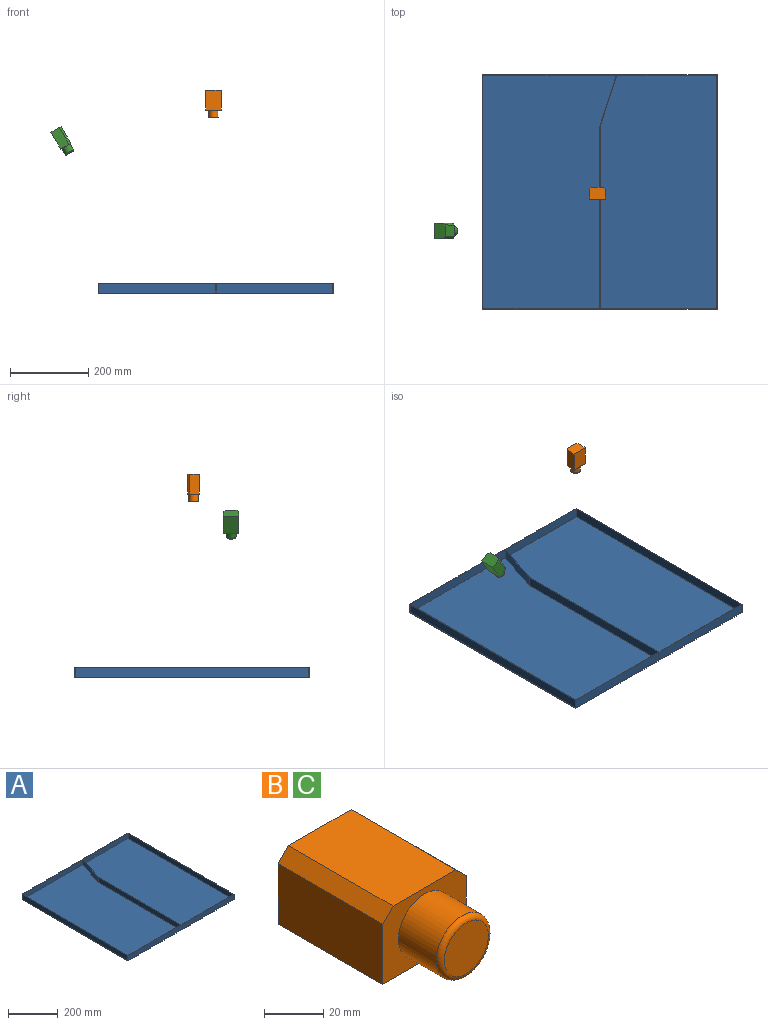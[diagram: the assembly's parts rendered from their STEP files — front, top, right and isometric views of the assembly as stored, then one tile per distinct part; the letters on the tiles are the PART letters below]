
ASSEMBLY  parts=3 mates=1
PART A: 18 faces, bbox 600x600x26 mm
  f0: plane 600x26mm, normal (1,0,0), area 15600mm2, adj f1,f3,f4,f15
  f1: plane 600x26mm, normal (0,1,0), area 15600mm2, adj f0,f2,f4,f15
  f2: plane 600x26mm, normal (-1,0,0), area 15600mm2, adj f1,f3,f4,f15
  f3: plane 600x26mm, normal (0,-1,0), area 15600mm2, adj f0,f2,f4,f15
  f4: plane 600x600mm, normal (0,0,-1), area 360000mm2, adj f0,f1,f2,f3
  f5: plane 298x25mm, normal (0,1,0), area 7450mm2, adj f6,f14,f15,f16
  f6: plane 466.35x25mm, normal (1,0,0), area 11658.9mm2, adj f5,f7,f15,f16
  f7: plane 131.65x42.43mm, normal (0.95,-0.31,0), area 3457.9mm2, adj f6,f8,f15,f16
  f8: plane 255.57x25mm, normal (0,-1,0), area 6389.2mm2, adj f7,f14,f15,f16
  f9: plane 131.49x42.38mm, normal (-0.95,0.31,0), area 3453.7mm2, adj f10,f13,f15,f17
  f10: plane 466.51x25mm, normal (-1,0,0), area 11662.8mm2, adj f9,f11,f15,f17
  f11: plane 299x25mm, normal (0,1,0), area 7475mm2, adj f10,f12,f15,f17
  f12: plane 598x25mm, normal (1,0,0), area 14950mm2, adj f11,f13,f15,f17
  f13: plane 341.38x25mm, normal (0,-1,0), area 8534.5mm2, adj f9,f12,f15,f17
  f14: plane 598x25mm, normal (-1,0,0), area 14950mm2, adj f5,f8,f15,f16
  f15: plane 600x600mm, normal (0,0,1), area 3000.7mm2, adj f0,f1,f2,f3,f5,f6,f7,f8
  f16: plane 598x298mm, normal (0,0,1), area 175411mm2, adj f5,f6,f7,f8,f14
  f17: plane 598x341.38mm, normal (0,0,1), area 181588.3mm2, adj f9,f10,f11,f12,f13
PART B: 11 faces, bbox 40x70x30 mm
  f0: plane 50x25mm, normal (1,0,0), area 1250mm2, adj f3,f4,f5,f9
  f1: plane 50x30mm, normal (0,0,1), area 1500mm2, adj f4,f5,f9,f10
  f2: plane 50x25mm, normal (-1,0,0), area 1250mm2, adj f3,f4,f5,f10
  f3: plane 50x40mm, normal (0,0,-1), area 2000mm2, adj f0,f2,f4,f5
  f4: plane 40x30mm, normal (0,-1,0), area 684.1mm2, adj f0,f1,f2,f3,f6,f9,f10
  f5: plane 40x30mm, normal (0,1,0), area 1175mm2, adj f0,f1,f2,f3,f9,f10
  f6: cylinder r=12.5mm len=25mm, axis (0,1,0), area 1413.7mm2, adj f4,f8
  f7: plane 21x21mm, normal (0,-1,0), area 346.4mm2, adj f8
  f8: torus R=10.5mm, axis (0,-1,0), area 232.4mm2, adj f6,f7
  f9: plane 50x5mm, normal (0.71,0,0.71), area 353.6mm2, adj f0,f1,f4,f5
  f10: plane 50x5mm, normal (-0.71,0,0.71), area 353.6mm2, adj f1,f2,f4,f5
PART C: same geometry as B
PLACE A t=(0.61,-0.34,-14.04)mm fixed
PLACE B rot(axis=(0,0.71,0.71),180deg) t=(-5.24,-4.4,504.96)mm
PLACE C rot(axis=(0.45,0.45,0.77),104.5deg) t=(-407.62,-100.39,405.7)mm
MATE parallel A.f16 <-> B.f6  axis (0,0,1) through (152.76,-4.4,-13.04)mm
